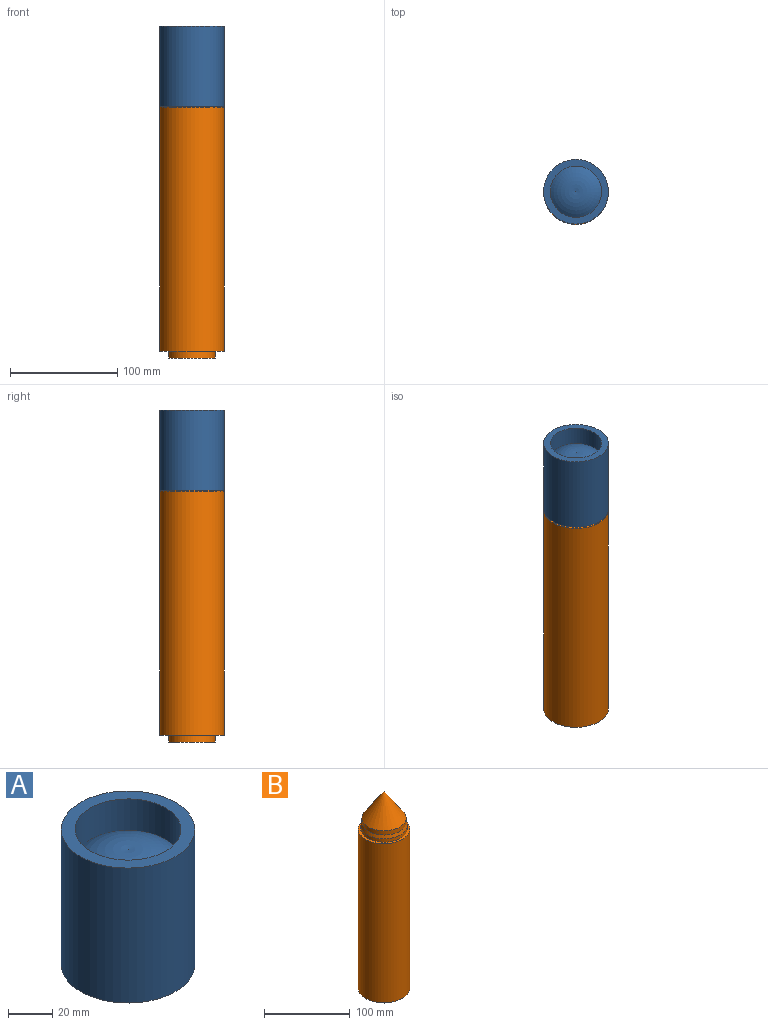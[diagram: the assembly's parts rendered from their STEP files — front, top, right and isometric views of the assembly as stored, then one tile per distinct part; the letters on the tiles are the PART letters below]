
ASSEMBLY  parts=2 mates=1
PART A: 9 faces, bbox 60.3x60.3x74.6 mm
  f0: torus R=4.74mm, axis (0,0,1), area 1985.5mm2, adj f4
  f1: plane 60.33x60.33mm, normal (0,0,-1), area 461.1mm2, adj f2,f6
  f2: cylinder r=30.16mm len=74.61mm, axis (0,0,1), area 14140.3mm2, adj f1,f3
  f3: plane 60.33x60.33mm, normal (0,0,1), area 1060.3mm2, adj f2,f4
  f4: cylinder r=23.92mm len=47.84mm, axis (0,0,1), area 2624.7mm2, adj f0,f3
  f5: torus R=4.74mm, axis (0,0,1), area 2619.7mm2, adj f8
  f6: cylinder r=27.62mm len=72.07mm, axis (0,0,1), area 12508.7mm2, adj f1,f7
  f7: plane 55.25x55.25mm, normal (0,0,-1), area 197.2mm2, adj f6,f8
  f8: cylinder r=26.46mm len=52.92mm, axis (0,0,1), area 3485.2mm2, adj f5,f7
PART B: 9 faces, bbox 60.3x60.3x287.3 mm
  f0: plane 60.33x60.33mm, normal (0,0,-1), area 1409mm2, adj f1,f8
  f1: cylinder r=30.16mm len=227.01mm, axis (0,0,1), area 43022.6mm2, adj f0,f2
  f2: plane 60.33x60.33mm, normal (0,0,1), area 570mm2, adj f1,f3
  f3: cylinder r=26.99mm len=53.98mm, axis (0,0,1), area 807.6mm2, adj f2,f4
  f4: cone r=26.99mm half-angle=15.8deg, axis (0,0,-1), area 788.1mm2, adj f3,f5
  f5: cylinder r=25.69mm len=51.37mm, axis (0,0,1), area 975mm2, adj f4,f6
  f6: cone r=0mm half-angle=33.6deg, axis (0,0,-1), area 3741mm2, adj f5
  f7: plane 42.95x42.95mm, normal (0,0,-1), area 1449.1mm2, adj f8
  f8: cylinder r=21.48mm len=42.95mm, axis (0,0,1), area 857.3mm2, adj f0,f7
PLACE A t=(-116.58,-135.16,102.13)mm
PLACE B rot(axis=(0,0,1),0deg) t=(-45.53,-135.16,49.16)mm
MATE slider A.f2 <-> B.f6  axis (0,0,-1) through (-77.09,-135.16,44.66)mm
